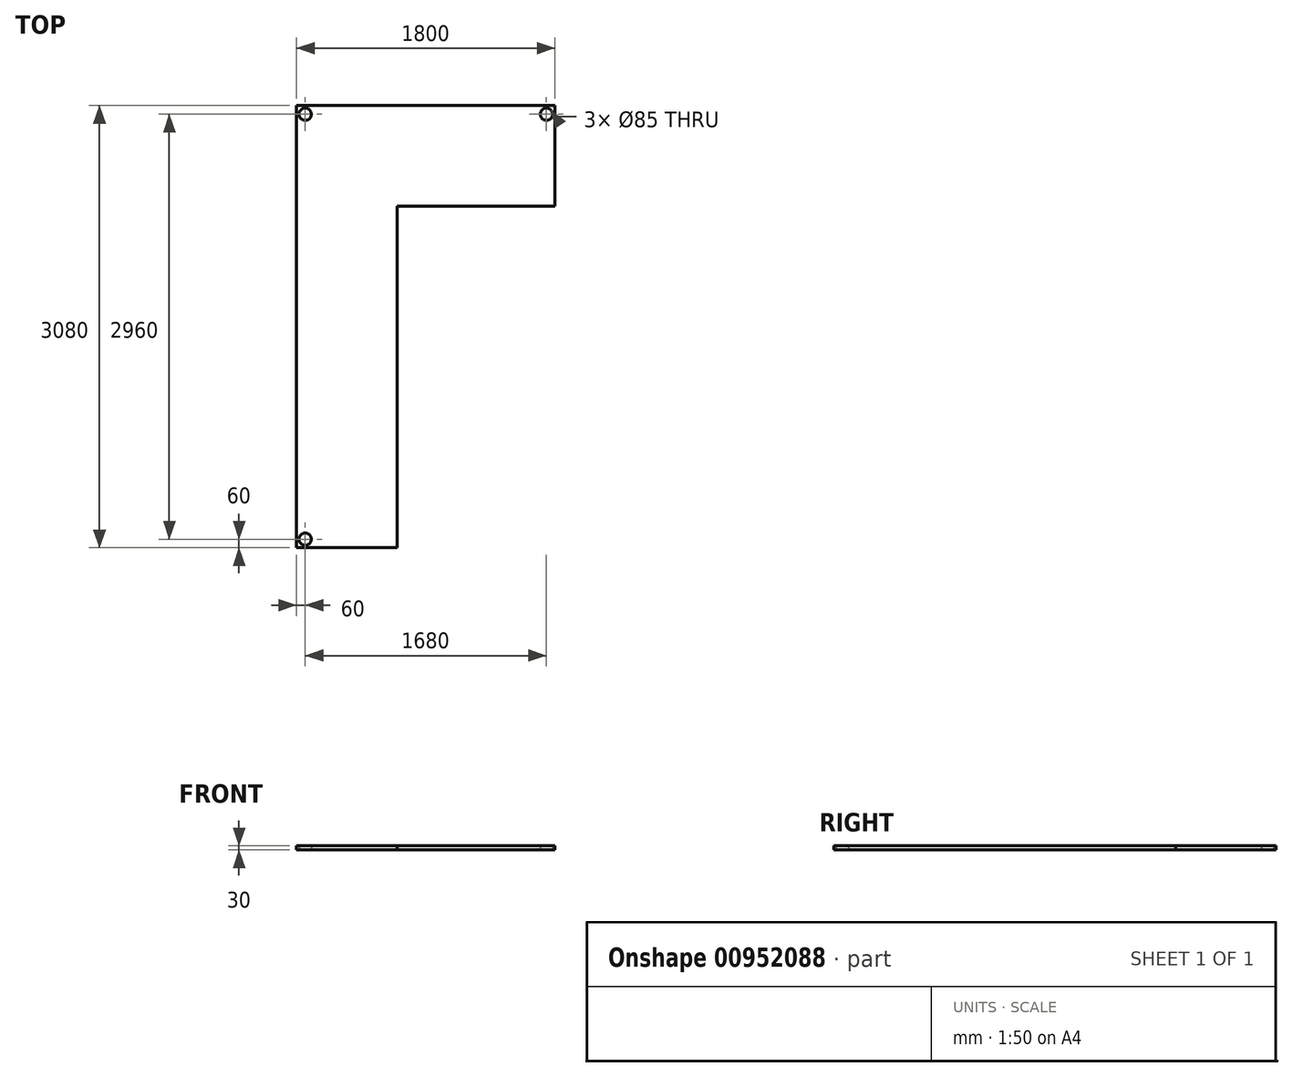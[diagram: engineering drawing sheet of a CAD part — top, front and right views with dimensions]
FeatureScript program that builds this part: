
annotation { "Feature Type Name" : "Feature", "Feature Type Description" : "" }
export const myFeature = defineFeature(function(context is Context, id is Id, definition is map)
    precondition{}
    {
        {
            var Q0;
            Q0=qCreatedBy(makeId("Top.planeOp"),FACE);
            var sketch = newSketch(context, id + "F0", { "sketchPlane" : qUnion([Q0])});
            skLineSegment(sketch, "E0.bottom", {"start": v(900, 350) * mm, "end": v(-900, 350) * mm});
            skLineSegment(sketch, "E0.top", {"start": v(900, -350) * mm, "end": v(-900, -350) * mm});
            skLineSegment(sketch, "E0.left", {"start": v(900, 350) * mm, "end": v(900, -350) * mm});
            skLineSegment(sketch, "E0.right", {"start": v(-900, 350) * mm, "end": v(-900, -350) * mm});
            skPoint(sketch, "E0.middle", {"position": v(0, 0) * mm});
            skCircle(sketch, "E1", {"center": v(-840, 290) * mm, "radius": 42.5 * mm});
            skCircle(sketch, "E2", {"center": v(840, 290) * mm, "radius": 42.5 * mm});
            skLineSegment(sketch, "E3.bottom", {"start": v(-900, -350) * mm, "end": v(-200, -350) * mm});
            skLineSegment(sketch, "E3.top", {"start": v(-900, -2730) * mm, "end": v(-200, -2730) * mm});
            skLineSegment(sketch, "E3.left", {"start": v(-900, -350) * mm, "end": v(-900, -2730) * mm});
            skLineSegment(sketch, "E3.right", {"start": v(-200, -350) * mm, "end": v(-200, -2730) * mm});
            skCircle(sketch, "E4", {"center": v(-840, -2670) * mm, "radius": 42.5 * mm});
            skSolve(sketch);
        }
        {
            var Q0;
            Q0 = qSketchRegion(id + "F0", true);
            extrude(context, id + "F1", {"entities" : qUnion([Q0]), "depth" : 30 * mm, "offsetDistance" : 25 * mm});
        }
    });
